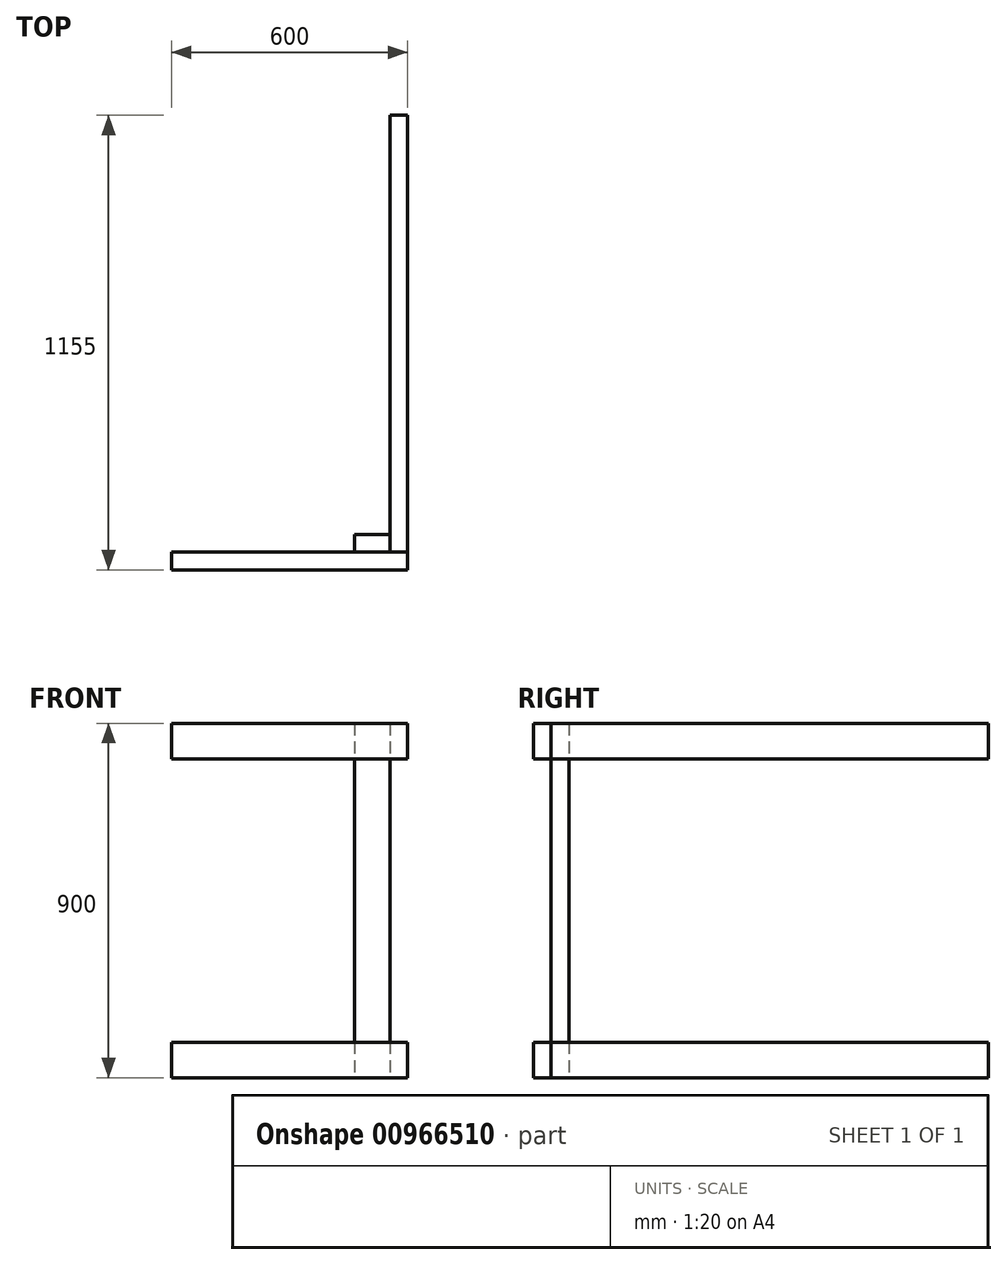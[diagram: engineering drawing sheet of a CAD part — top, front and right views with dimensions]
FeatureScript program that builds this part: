
annotation { "Feature Type Name" : "Feature", "Feature Type Description" : "" }
export const myFeature = defineFeature(function(context is Context, id is Id, definition is map)
    precondition{}
    {
        {
            var Q0;
            Q0=qCreatedBy(makeId("Top.planeOp"),FACE);
            var sketch = newSketch(context, id + "F0", { "sketchPlane" : qUnion([Q0])});
            skLineSegment(sketch, "E0.bottom", {"start": v(0, 0) * mm, "end": v(45, 0) * mm});
            skLineSegment(sketch, "E0.top", {"start": v(0, 1110) * mm, "end": v(45, 1110) * mm});
            skLineSegment(sketch, "E0.left", {"start": v(0, 0) * mm, "end": v(0, 1110) * mm});
            skLineSegment(sketch, "E0.right", {"start": v(45, 0) * mm, "end": v(45, 1110) * mm});
            skSolve(sketch);
        }
        {
            var Q0;
            Q0 = qSketchRegion(id + "F0", true);
            extrude(context, id + "F1", {"entities" : qUnion([Q0]), "depth" : 90 * mm, "offsetDistance" : 25 * mm});
        }
        {
            var Q0;
            Q0=qCreatedBy(makeId("Top.planeOp"),FACE);
            var sketch = newSketch(context, id + "F2", { "sketchPlane" : qUnion([Q0])});
            skLineSegment(sketch, "E1.bottom", {"start": v(45, 0) * mm, "end": v(-555, 0) * mm});
            skLineSegment(sketch, "E1.top", {"start": v(45, -45) * mm, "end": v(-555, -45) * mm});
            skLineSegment(sketch, "E1.left", {"start": v(45, 0) * mm, "end": v(45, -45) * mm});
            skLineSegment(sketch, "E1.right", {"start": v(-555, 0) * mm, "end": v(-555, -45) * mm});
            skSolve(sketch);
        }
        {
            var Q0;
            Q0 = qSketchRegion(id + "F2", true);
            extrude(context, id + "F3", {"entities" : qUnion([Q0]), "depth" : 90 * mm, "offsetDistance" : 25 * mm});
        }
        {
            var Q0;
            Q0=qCreatedBy(makeId("Top.planeOp"),FACE);
            var sketch = newSketch(context, id + "F4", { "sketchPlane" : qUnion([Q0])});
            skLineSegment(sketch, "E2.bottom", {"start": v(0, 0) * mm, "end": v(-90, 0) * mm});
            skLineSegment(sketch, "E2.top", {"start": v(0, 45) * mm, "end": v(-90, 45) * mm});
            skLineSegment(sketch, "E2.left", {"start": v(0, 0) * mm, "end": v(0, 45) * mm});
            skLineSegment(sketch, "E2.right", {"start": v(-90, 0) * mm, "end": v(-90, 45) * mm});
            skSolve(sketch);
        }
        {
            var Q0;
            Q0 = qSketchRegion(id + "F4", true);
            extrude(context, id + "F5", {"entities" : qUnion([Q0]), "depth" : 900 * mm, "offsetDistance" : 25 * mm});
        }
        {
            var Q0;
            Q0=makeQuery(id+"F5.opExtrude","CAP_FACE",FACE,{"disambiguationData":[OSD([sQuery(id+"F4.wireOp",EDGE,"E2.bottom"),sQuery(id+"F4.wireOp",EDGE,"E2.top"),sQuery(id+"F4.wireOp",EDGE,"E2.left"),sQuery(id+"F4.wireOp",EDGE,"E2.right")])],"isStart":false});
            var sketch = newSketch(context, id + "F6", { "sketchPlane" : qUnion([Q0])});
            skLineSegment(sketch, "E3.bottom", {"start": v(0, 0) * mm, "end": v(45, 0) * mm});
            skLineSegment(sketch, "E3.top", {"start": v(0, 1110) * mm, "end": v(45, 1110) * mm});
            skLineSegment(sketch, "E3.left", {"start": v(0, 0) * mm, "end": v(0, 1110) * mm});
            skLineSegment(sketch, "E3.right", {"start": v(45, 0) * mm, "end": v(45, 1110) * mm});
            skSolve(sketch);
        }
        {
            var Q0;
            Q0 = qSketchRegion(id + "F6", true);
            extrude(context, id + "F7", {"entities" : qUnion([Q0]), "oppositeDirection" : true, "depth" : 90 * mm, "offsetDistance" : 25 * mm});
        }
        {
            var Q0;
            Q0=makeQuery(id+"F5.opExtrude","CAP_FACE",FACE,{"disambiguationData":[OSD([sQuery(id+"F4.wireOp",EDGE,"E2.bottom"),sQuery(id+"F4.wireOp",EDGE,"E2.top"),sQuery(id+"F4.wireOp",EDGE,"E2.left"),sQuery(id+"F4.wireOp",EDGE,"E2.right")])],"isStart":false});
            var sketch = newSketch(context, id + "F8", { "sketchPlane" : qUnion([Q0])});
            skLineSegment(sketch, "E4.bottom", {"start": v(45, 0) * mm, "end": v(-555, 0) * mm});
            skLineSegment(sketch, "E4.top", {"start": v(45, -45) * mm, "end": v(-555, -45) * mm});
            skLineSegment(sketch, "E4.left", {"start": v(45, 0) * mm, "end": v(45, -45) * mm});
            skLineSegment(sketch, "E4.right", {"start": v(-555, 0) * mm, "end": v(-555, -45) * mm});
            skSolve(sketch);
        }
        {
            var Q0;
            Q0 = qSketchRegion(id + "F8", true);
            extrude(context, id + "F9", {"entities" : qUnion([Q0]), "oppositeDirection" : true, "depth" : 90 * mm, "offsetDistance" : 25 * mm});
        }
    });
